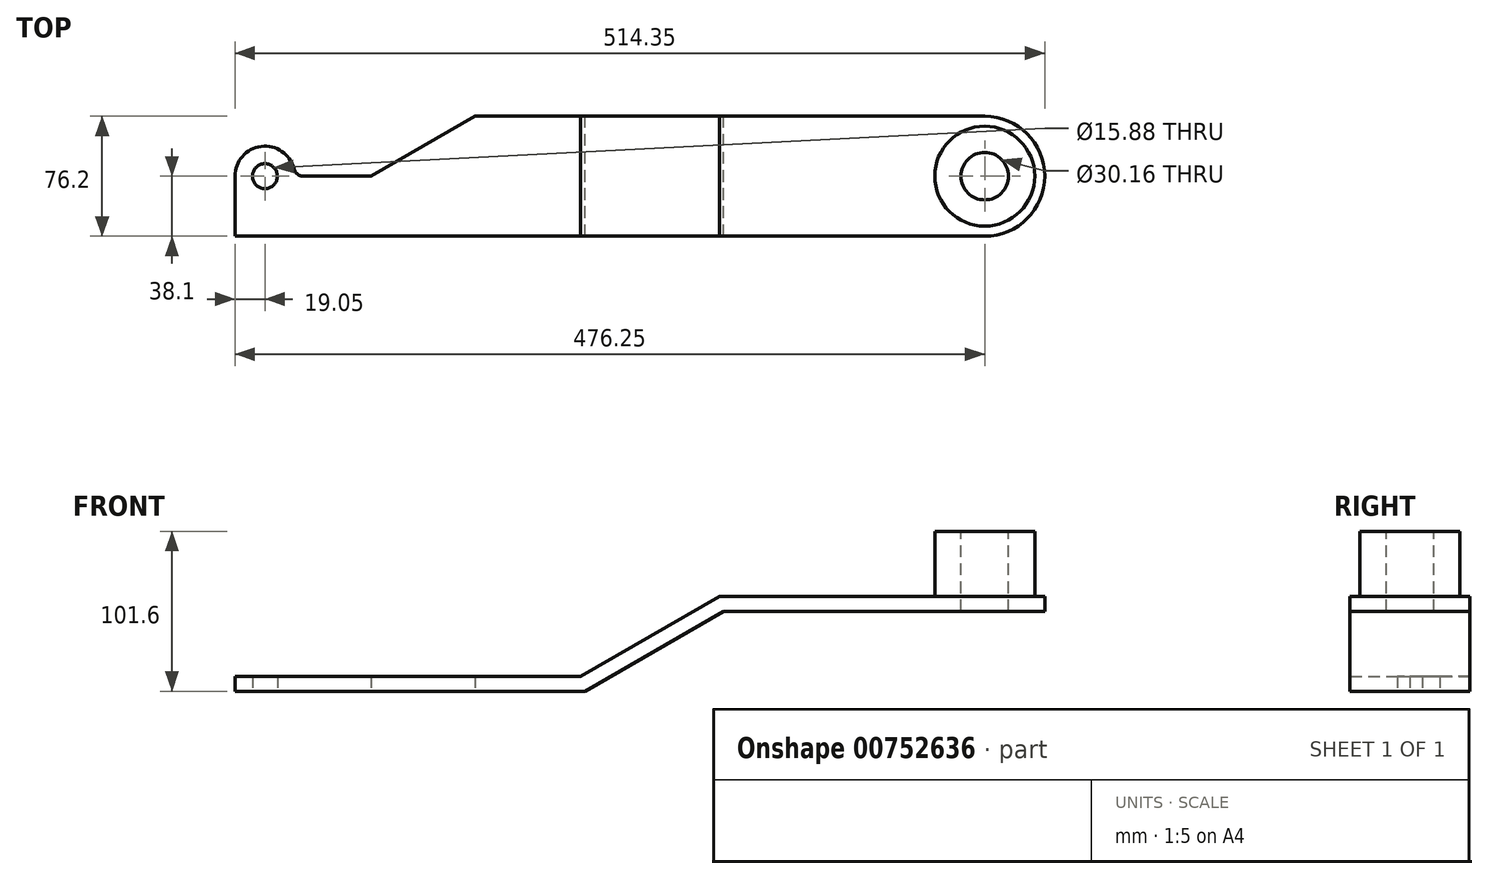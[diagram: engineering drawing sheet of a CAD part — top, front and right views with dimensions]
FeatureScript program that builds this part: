
annotation { "Feature Type Name" : "Feature", "Feature Type Description" : "" }
export const myFeature = defineFeature(function(context is Context, id is Id, definition is map)
    precondition{}
    {
        {
            var Q0;
            Q0=qCreatedBy(makeId("Top.planeOp"),FACE);
            var sketch = newSketch(context, id + "F0", { "sketchPlane" : qUnion([Q0])});
            skLineSegment(sketch, "E0.bottom", {"start": v(0, -38.1) * mm, "end": v(-476.25, -38.1) * mm});
            skLineSegment(sketch, "E0.top", {"start": v(0, 38.1) * mm, "end": v(-180.62, 38.1) * mm});
            skLineSegment(sketch, "E1", {"start": v(0, 0) * mm, "end": v(-432.6, 0) * mm, "construction": true});
            skCircle(sketch, "E2", {"center": v(0, 0) * mm, "radius": 304.8 * mm, "construction": true});
            skLineSegment(sketch, "E3", {"start": v(0, 0) * mm, "end": v(-323.29, -323.29) * mm, "construction": true});
            skLineSegment(sketch, "E4", {"start": v(0, 0) * mm, "end": v(-323.29, 323.29) * mm, "construction": true});
            skLineSegment(sketch, "E5", {"start": v(-215.53, 215.53) * mm, "end": v(-215.53, -215.53) * mm, "construction": true});
            skCircle(sketch, "E6.0", {"center": v(0, 0) * mm, "radius": 457.2 * mm, "construction": true});
            skLineSegment(sketch, "E7", {"start": v(-323.29, 323.29) * mm, "end": v(-323.29, -323.29) * mm, "construction": true});
            skArc(sketch, "E8", {"start": v(-438.75, 4.76) * mm, "mid": v(-459.6, 18.9) * mm, "end": v(-476.25, 0) * mm});
            skLineSegment(sketch, "E9", {"start": v(-476.25, 0) * mm, "end": v(-476.25, -38.1) * mm});
            skLineSegment(sketch, "E10", {"start": v(-180.62, 38.1) * mm, "end": v(-323.74, 38.1) * mm});
            skPoint(sketch, "E11.orphan", {"position": v(-389.73, 71.95) * mm});
            skLineSegment(sketch, "E12", {"start": v(-389.73, 0) * mm, "end": v(-432.6, 0) * mm});
            skArc(sketch, "E13.filletArc", {"start": v(-438.75, 4.76) * mm, "mid": v(-436.5, 1.33) * mm, "end": v(-432.6, 0) * mm});
            skLineSegment(sketch, "E14", {"start": v(-389.73, 0) * mm, "end": v(-323.74, 38.1) * mm});
            skPoint(sketch, "E15.orphan", {"position": v(-389.73, 38.1) * mm});
            skCircle(sketch, "E16", {"center": v(-457.2, 0) * mm, "radius": 7.94 * mm});
            skArc(sketch, "E17", {"start": v(0, -38.1) * mm, "mid": v(38.1, 0) * mm, "end": v(0, 38.1) * mm});
            skSolve(sketch);
        }
        {
            var Q0;
            Q0 = qSketchRegion(id + "F0", true);
            extrude(context, id + "F1", {"entities" : qUnion([Q0]), "depth" : 9.52 * mm, "offsetDistance" : 25.4 * mm, "hasSecondDirection" : true, "secondDirectionOppositeDirection" : true, "secondDirectionDepth" : 50.8 * mm});
        }
        {
            var Q0;
            Q0=makeQuery(id+"F1.opExtrude","CAP_FACE",FACE,{"disambiguationData":[OSD([sQuery(id+"F0.wireOp",EDGE,"E0.bottom"),sQuery(id+"F0.wireOp",EDGE,"E0.top"),sQuery(id+"F0.wireOp",EDGE,"E8"),sQuery(id+"F0.wireOp",EDGE,"E9"),sQuery(id+"F0.wireOp",EDGE,"E10"),sQuery(id+"F0.wireOp",EDGE,"E12"),sQuery(id+"F0.wireOp",EDGE,"E13.filletArc"),sQuery(id+"F0.wireOp",EDGE,"E14"),sQuery(id+"F0.wireOp",EDGE,"E16"),sQuery(id+"F0.wireOp",EDGE,"E17")])],"isStart":false});
            var sketch = newSketch(context, id + "F2", { "sketchPlane" : qUnion([Q0])});
            skCircle(sketch, "E18", {"center": v(0, 0) * mm, "radius": 31.75 * mm});
            skSolve(sketch);
        }
        {
            var Q0;
            Q0 = qSketchRegion(id + "F2", true);
            extrude(context, id + "F3", {"entities" : qUnion([Q0]), "operationType" : NewBodyOperationType.ADD, "depth" : 41.27 * mm, "offsetDistance" : 25.4 * mm});
        }
        {
            var Q0;
            Q0=makeQuery(id+"F3.opExtrude","CAP_FACE",FACE,{"disambiguationData":[OSD([sQuery(id+"F2.wireOp",EDGE,"E18")])],"isStart":false});
            var sketch = newSketch(context, id + "F4", { "sketchPlane" : qUnion([Q0])});
            skCircle(sketch, "E19", {"center": v(0, 0) * mm, "radius": 15.08 * mm});
            skSolve(sketch);
        }
        {
            var Q0;
            Q0 = qSketchRegion(id + "F4", true);
            extrude(context, id + "F5", {"entities" : qUnion([Q0]), "operationType" : NewBodyOperationType.REMOVE, "endBound" : BoundingType.THROUGH_ALL, "oppositeDirection" : true, "depth" : 25.4 * mm, "offsetDistance" : 25.4 * mm});
        }
        {
            var Q0;
            Q0=makeQuery(id+"F1.opExtrude","SWEPT_FACE",FACE,{"disambiguationData":[OSD([sQuery(id+"F0.wireOp",EDGE,"E0.top"),sQuery(id+"F0.wireOp",EDGE,"E10")])]});
            var sketch = newSketch(context, id + "F6", { "sketchPlane" : qUnion([Q0])});
            skLineSegment(sketch, "E20.bottom", {"start": v(254, -50.8) * mm, "end": v(-101.6, -50.8) * mm});
            skLineSegment(sketch, "E20.top", {"start": v(166.01, 0) * mm, "end": v(-101.6, 0) * mm});
            skLineSegment(sketch, "E20.right", {"start": v(-101.6, -50.8) * mm, "end": v(-101.6, 0) * mm});
            skLineSegment(sketch, "E21", {"start": v(254, -50.8) * mm, "end": v(166.01, 0) * mm});
            skLineSegment(sketch, "E22.bottom", {"start": v(168.56, 9.52) * mm, "end": v(524.16, 9.52) * mm});
            skLineSegment(sketch, "E22.top", {"start": v(256.55, -41.28) * mm, "end": v(524.16, -41.28) * mm});
            skLineSegment(sketch, "E22.right", {"start": v(524.16, 9.52) * mm, "end": v(524.16, -41.28) * mm});
            skLineSegment(sketch, "E23", {"start": v(168.56, 9.53) * mm, "end": v(256.55, -41.28) * mm});
            skSolve(sketch);
        }
        {
            var Q0;
            Q0 = qSketchRegion(id + "F6", true);
            extrude(context, id + "F7", {"entities" : qUnion([Q0]), "operationType" : NewBodyOperationType.REMOVE, "endBound" : BoundingType.THROUGH_ALL, "oppositeDirection" : true, "depth" : 25.4 * mm, "offsetDistance" : 25.4 * mm});
        }
    });
